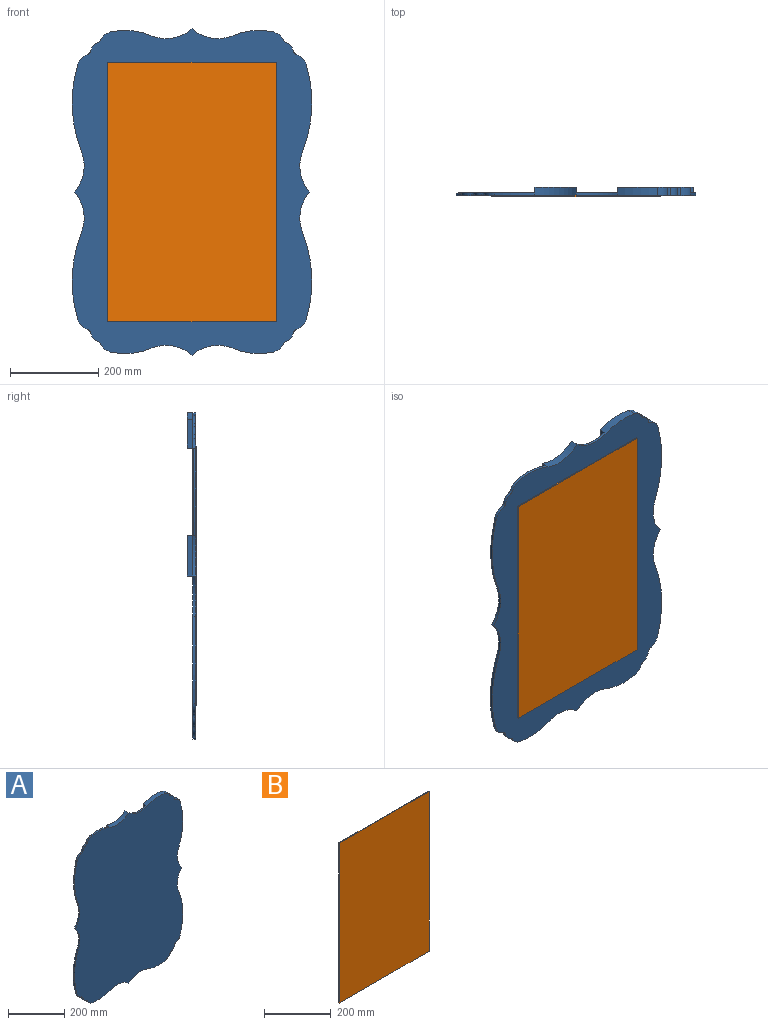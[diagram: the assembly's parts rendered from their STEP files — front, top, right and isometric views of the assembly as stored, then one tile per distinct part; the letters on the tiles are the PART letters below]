
ASSEMBLY  parts=2 mates=1
PART A: 67 faces, bbox 543.5x19.1x739.8 mm
  f0: plane 93.1x79.81mm, normal (0,1,0), area 5850.4mm2, adj f38,f51,f55,f63
  f1: plane 198.75x178.67mm, normal (0,1,0), area 34367.7mm2, adj f31,f44,f56,f64
  f2: plane 198.75x93.1mm, normal (0,1,0), area 18504.1mm2, adj f48,f52,f59,f62
  f3: plane 165.92x76.27mm, normal (0,1,0), area 9712.3mm2, adj f5,f6,f7,f8,f9,f40,f53,f58
  f4: plane 543.54x461.21mm, normal (0,1,0), area 205281.8mm2, adj f11,f12,f13,f14,f15,f16,f17,f18
  f5: cylinder r=31.75mm len=21.98mm, axis (0,1,0), area 185.4mm2, adj f3,f6,f40,f41
  f6: cylinder r=12.7mm len=6.92mm, axis (0,1,0), area 61.7mm2, adj f3,f5,f7,f41
  f7: cylinder r=25.4mm len=17.98mm, axis (0,1,0), area 157.1mm2, adj f3,f6,f8,f41
  f8: cylinder r=12.7mm len=9.31mm, axis (0,1,0), area 84.8mm2, adj f3,f7,f9,f41
  f9: cylinder r=31.75mm len=21.31mm, axis (0,1,0), area 199mm2, adj f3,f8,f10,f41,f58
  f10: cylinder r=304.8mm len=198.75mm, axis (0,1,0), area 965mm2, adj f9,f11,f41,f61
  f11: cylinder r=88.9mm len=91.33mm, axis (0,1,0), area 619.4mm2, adj f4,f10,f12,f41,f60
  f12: cylinder r=88.9mm len=91.33mm, axis (0,1,0), area 619.4mm2, adj f4,f11,f13,f41
  f13: cylinder r=304.8mm len=198.75mm, axis (0,1,0), area 1286.7mm2, adj f4,f12,f14,f41
  f14: cylinder r=31.75mm len=21.31mm, axis (0,1,0), area 199mm2, adj f4,f13,f15,f41
  f15: cylinder r=12.7mm len=9.31mm, axis (0,1,0), area 84.8mm2, adj f4,f14,f16,f41
  f16: cylinder r=25.4mm len=17.98mm, axis (0,1,0), area 157.1mm2, adj f4,f15,f17,f41
  f17: cylinder r=12.7mm len=6.92mm, axis (0,1,0), area 61.7mm2, adj f4,f16,f18,f41
  f18: cylinder r=31.75mm len=21.98mm, axis (0,1,0), area 185.4mm2, adj f4,f17,f19,f41
  f19: cylinder r=152.4mm len=91.51mm, axis (0,1,0), area 592.7mm2, adj f4,f18,f20,f41
  f20: cylinder r=88.9mm len=93.1mm, axis (0,1,0), area 631.6mm2, adj f4,f19,f21,f41
  f21: cylinder r=88.9mm len=93.1mm, axis (0,1,0), area 631.6mm2, adj f4,f20,f22,f41
  f22: cylinder r=152.4mm len=91.51mm, axis (0,1,0), area 592.7mm2, adj f4,f21,f23,f41
  f23: cylinder r=31.75mm len=21.98mm, axis (0,1,0), area 185.4mm2, adj f4,f22,f24,f41
  f24: cylinder r=12.7mm len=6.92mm, axis (0,1,0), area 61.7mm2, adj f4,f23,f25,f41
  f25: cylinder r=25.4mm len=17.98mm, axis (0,1,0), area 157.1mm2, adj f4,f24,f26,f41
  f26: cylinder r=12.7mm len=9.31mm, axis (0,1,0), area 84.8mm2, adj f4,f25,f27,f41
  f27: cylinder r=31.75mm len=21.31mm, axis (0,1,0), area 199mm2, adj f4,f26,f28,f41
  f28: cylinder r=304.8mm len=198.75mm, axis (0,1,0), area 1286.7mm2, adj f4,f27,f29,f41
  f29: cylinder r=88.9mm len=91.33mm, axis (0,1,0), area 619.4mm2, adj f4,f28,f30,f41
  f30: cylinder r=88.9mm len=91.33mm, axis (0,1,0), area 1858.3mm2, adj f29,f31,f41,f42,f44,f45
  f31: cylinder r=304.8mm len=198.75mm, axis (0,1,0), area 1286.7mm2, adj f1,f30,f32,f41
  f32: cylinder r=31.75mm len=21.31mm, axis (0,1,0), area 597.1mm2, adj f31,f33,f41,f56,f57
  f33: cylinder r=12.7mm len=19.05mm, axis (0,1,0), area 254.4mm2, adj f32,f34,f41,f57
  f34: cylinder r=25.4mm len=19.05mm, axis (0,1,0), area 471.4mm2, adj f33,f35,f41,f57
  f35: cylinder r=12.7mm len=19.05mm, axis (0,1,0), area 185.2mm2, adj f34,f36,f41,f57
  f36: cylinder r=31.75mm len=21.98mm, axis (0,1,0), area 556.2mm2, adj f35,f37,f41,f57
  f37: cylinder r=152.4mm len=91.51mm, axis (0,1,0), area 1778mm2, adj f36,f38,f41,f55,f57
  f38: cylinder r=88.9mm len=93.1mm, axis (0,1,0), area 631.6mm2, adj f0,f37,f39,f41
  f39: cylinder r=88.9mm len=93.1mm, axis (0,1,0), area 1894.8mm2, adj f38,f40,f41,f51,f53,f54
  f40: cylinder r=152.4mm len=91.51mm, axis (0,1,0), area 592.7mm2, adj f3,f5,f39,f41
  f41: plane 739.78x543.54mm, normal (0,-1,0), area 364955mm2, adj f5,f6,f7,f8,f9,f10,f11,f12
  f42: plane 173.6x12.7mm, normal (0,0,-1), area 2204.7mm2, adj f4,f30,f43,f45
  f43: plane 91.33x12.7mm, normal (-1,0,0), area 1159.9mm2, adj f4,f42,f44,f45
  f44: plane 157.53x12.7mm, normal (0,0,1), area 2000.7mm2, adj f1,f30,f43,f45
  f45: plane 173.6x91.33mm, normal (0,1,0), area 14301.4mm2, adj f30,f42,f43,f44
  f46: plane 93.1x12.7mm, normal (0,0,-1), area 1182.4mm2, adj f4,f47,f49,f50
  f47: plane 91.33x12.7mm, normal (-1,0,0), area 1159.9mm2, adj f4,f46,f48,f50
  f48: plane 93.1x12.7mm, normal (0,0,1), area 1182.4mm2, adj f2,f47,f49,f50
  f49: plane 91.33x12.7mm, normal (1,0,0), area 1159.9mm2, adj f4,f46,f48,f50
  f50: plane 93.1x91.33mm, normal (0,1,0), area 8502.9mm2, adj f46,f47,f48,f49
  f51: plane 79.81x12.7mm, normal (1,0,0), area 1013.6mm2, adj f0,f39,f52,f54
  f52: plane 93.1x12.7mm, normal (0,0,-1), area 1182.4mm2, adj f2,f51,f53,f54
  f53: plane 64.47x12.7mm, normal (-1,0,0), area 818.8mm2, adj f3,f39,f52,f54
  f54: plane 93.1x79.81mm, normal (0,1,0), area 5850.4mm2, adj f39,f51,f52,f53
  f55: plane 64.47x12.7mm, normal (-1,0,0), area 818.8mm2, adj f0,f37,f56,f57
  f56: plane 165.92x12.7mm, normal (0,0,-1), area 2107.2mm2, adj f1,f32,f55,f57
  f57: plane 165.92x76.27mm, normal (0,1,0), area 9712.3mm2, adj f32,f33,f34,f35,f36,f37,f55,f56
  f58: plane 165.92x1.59mm, normal (0,0,-1), area 263.4mm2, adj f3,f9,f59,f61
  f59: plane 198.75x1.59mm, normal (-1,0,0), area 315.5mm2, adj f2,f58,f60,f61
  f60: plane 157.53x1.59mm, normal (0,0,1), area 250.1mm2, adj f4,f11,f59,f61
  f61: plane 198.75x178.67mm, normal (0,1,0), area 34367.7mm2, adj f10,f58,f59,f60
  f62: plane 198.75x1.59mm, normal (1,0,0), area 315.5mm2, adj f2,f63,f65,f66
  f63: plane 93.1x1.59mm, normal (0,0,-1), area 147.8mm2, adj f0,f62,f64,f66
  f64: plane 198.75x1.59mm, normal (-1,0,0), area 315.5mm2, adj f1,f63,f65,f66
  f65: plane 93.1x1.59mm, normal (0,0,1), area 147.8mm2, adj f4,f62,f64,f66
  f66: plane 198.75x93.1mm, normal (0,1,0), area 18504.1mm2, adj f62,f63,f64,f65
PART B: 6 faces, bbox 381x2.4x587.4 mm
  f0: plane 587.38x2.38mm, normal (1,0,0), area 1398.7mm2, adj f1,f3,f4,f5
  f1: plane 381x2.38mm, normal (0,0,1), area 907.3mm2, adj f0,f2,f4,f5
  f2: plane 587.38x2.38mm, normal (-1,0,0), area 1398.7mm2, adj f1,f3,f4,f5
  f3: plane 381x2.38mm, normal (0,0,-1), area 907.3mm2, adj f0,f2,f4,f5
  f4: plane 587.38x381mm, normal (0,-1,0), area 223789.9mm2, adj f0,f1,f2,f3
  f5: plane 587.38x381mm, normal (0,1,0), area 223789.9mm2, adj f0,f1,f2,f3
PLACE A t=(-221.18,-40.76,-344.26)mm
PLACE B t=(-221.18,-47.11,-344.26)mm
MATE fastened A.f41 <-> B.f5  axis (0,-1,0) through (-221.18,-47.11,-344.26)mm
